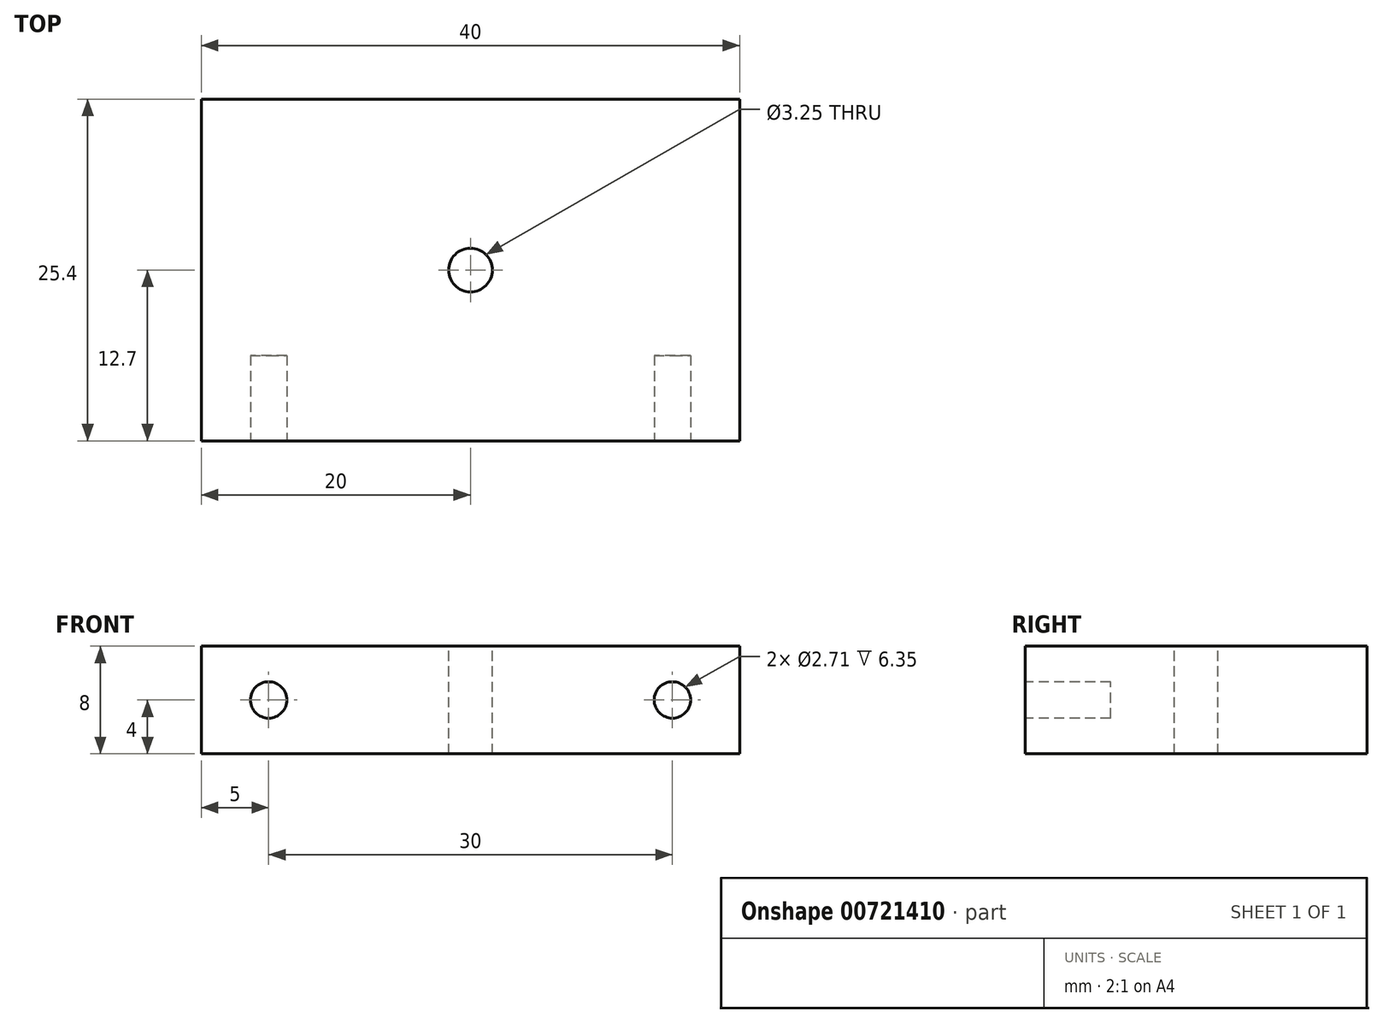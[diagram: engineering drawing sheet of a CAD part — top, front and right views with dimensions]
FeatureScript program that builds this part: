
annotation { "Feature Type Name" : "Feature", "Feature Type Description" : "" }
export const myFeature = defineFeature(function(context is Context, id is Id, definition is map)
    precondition{}
    {
        {
            var Q0;
            Q0=qCreatedBy(makeId("Top.planeOp"),FACE);
            var sketch = newSketch(context, id + "F0", { "sketchPlane" : qUnion([Q0])});
            skLineSegment(sketch, "E0.bottom", {"start": v(0, 0) * mm, "end": v(40, 0) * mm});
            skLineSegment(sketch, "E0.top", {"start": v(0, 25.4) * mm, "end": v(40, 25.4) * mm});
            skLineSegment(sketch, "E0.left", {"start": v(0, 0) * mm, "end": v(0, 25.4) * mm});
            skLineSegment(sketch, "E0.right", {"start": v(40, 0) * mm, "end": v(40, 25.4) * mm});
            skSolve(sketch);
        }
        {
            var Q0;
            Q0=makeQuery(id+"F0.imprint","IMPRINT",FACE,{"disambiguationData":[TD([[makeQuery(id+"F0.imprint","IMPRINT",EDGE,{"derivedFrom":sQuery(id+"F0.wireOp",EDGE,"E0.bottom")}),1.0]])]});
            extrude(context, id + "F1", {"entities" : qUnion([Q0]), "depth" : 8 * mm, "offsetDistance" : 25.4 * mm});
        }
        {
            var Q0;
            Q0=makeQuery(id+"F1.opExtrude","CAP_FACE",FACE,{"disambiguationData":[OSD([sQuery(id+"F0.wireOp",EDGE,"E0.bottom"),sQuery(id+"F0.wireOp",EDGE,"E0.top"),sQuery(id+"F0.wireOp",EDGE,"E0.left"),sQuery(id+"F0.wireOp",EDGE,"E0.right")])],"isStart":false});
            var sketch = newSketch(context, id + "F2", { "sketchPlane" : qUnion([Q0])});
            skCircle(sketch, "E1", {"center": v(20, 12.7) * mm, "radius": 1.63 * mm});
            skPoint(sketch, "E1.centerSnap0", {"position": v(0, 12.7) * mm});
            skPoint(sketch, "E1.centerSnap1", {"position": v(20, 25.4) * mm});
            skSolve(sketch);
        }
        {
            var Q0;
            Q0=makeQuery(id+"F1.opExtrude","SWEPT_FACE",FACE,{"disambiguationData":[OSD([sQuery(id+"F0.wireOp",EDGE,"E0.bottom")])]});
            var sketch = newSketch(context, id + "F3", { "sketchPlane" : qUnion([Q0])});
            skCircle(sketch, "E2", {"center": v(5, 4) * mm, "radius": 1.35 * mm});
            skPoint(sketch, "E2.centerSnap0", {"position": v(0, 4) * mm});
            skCircle(sketch, "E3", {"center": v(35, 4) * mm, "radius": 1.35 * mm});
            skPoint(sketch, "E3.centerSnap0", {"position": v(40, 4) * mm});
            skSolve(sketch);
        }
        {
            var Q0;
            Q0=makeQuery(id+"F3.imprint","IMPRINT",FACE,{"disambiguationData":[TD([[makeQuery(id+"F3.imprint","IMPRINT",EDGE,{"derivedFrom":sQuery(id+"F3.wireOp",EDGE,"E2")}),1.0]])]});
            var Q1;
            Q1=makeQuery(id+"F3.imprint","IMPRINT",FACE,{"disambiguationData":[TD([[makeQuery(id+"F3.imprint","IMPRINT",EDGE,{"derivedFrom":sQuery(id+"F3.wireOp",EDGE,"E3")}),1.0]])]});
            extrude(context, id + "F4", {"entities" : qUnion([Q0, Q1]), "operationType" : NewBodyOperationType.REMOVE, "oppositeDirection" : true, "depth" : 6.35 * mm, "offsetDistance" : 25.4 * mm});
        }
        {
            var Q0;
            Q0=makeQuery(id+"F2.imprint","IMPRINT",FACE,{"disambiguationData":[TD([[makeQuery(id+"F2.imprint","IMPRINT",EDGE,{"derivedFrom":sQuery(id+"F2.wireOp",EDGE,"E1")}),1.0]])]});
            extrude(context, id + "F5", {"entities" : qUnion([Q0]), "operationType" : NewBodyOperationType.REMOVE, "oppositeDirection" : true, "depth" : 25.4 * mm, "offsetDistance" : 25.4 * mm});
        }
    });
